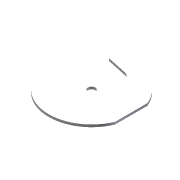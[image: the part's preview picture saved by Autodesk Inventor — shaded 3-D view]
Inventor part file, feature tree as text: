
AUTODESK INVENTOR PART (.ipt)
format: ipt  version: 2012 (Build 160160000, 160)  size: 101,888 bytes
history: native  units: mm
features: extrude x1, sketch x1
ambient origin geometry x8: Origin, YZ Plane, XZ Plane, XY Plane, X Axis, Y Axis, Z Axis, Center Point
feature tree (2):
  extrude  "Extrusion3"  Depth=9.18mm
  sketch  "Sketch1"  dims[d0=108.0mm d1=9.18mm d4=20.0mm d5=30.0mm d12=50.0mm d13=2.0mm d14=54.0mm d15=54.0mm d16=20.0mm d17=3.0mm d18=0.0mm d19=13.596115mm d20=50.0mm]
